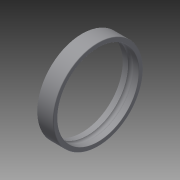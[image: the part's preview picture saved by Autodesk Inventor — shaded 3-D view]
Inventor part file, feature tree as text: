
AUTODESK INVENTOR PART (.ipt)
format: ipt  version: 2014 SP2 (Build 180246200, 246)  size: 148,992 bytes
history: native  units: mm
features: other x7, revolve x1, sketch x1
ambient origin geometry x8: Origin, YZ Plane, XZ Plane, XY Plane, X Axis, Y Axis, Z Axis, Center Point
bodies: Solid1 (feature_tree)
feature tree (9):
  revolve  "Revolution1"  [1 undecoded]
  other  "1_XY"
  other  "1_YZ"
  other  "1_ZX"
  other  "1_X"
  other  "1_Y"
  other  "1_Z"
  other  "1_Center"
  sketch  "Sketch_1"  dims[d0=360.0deg]
note: 1 required parameter value undecoded (feature->parameter linkage not recoverable at this tier; creation-order binding heuristic only, values carry confidence <= 0.55)
